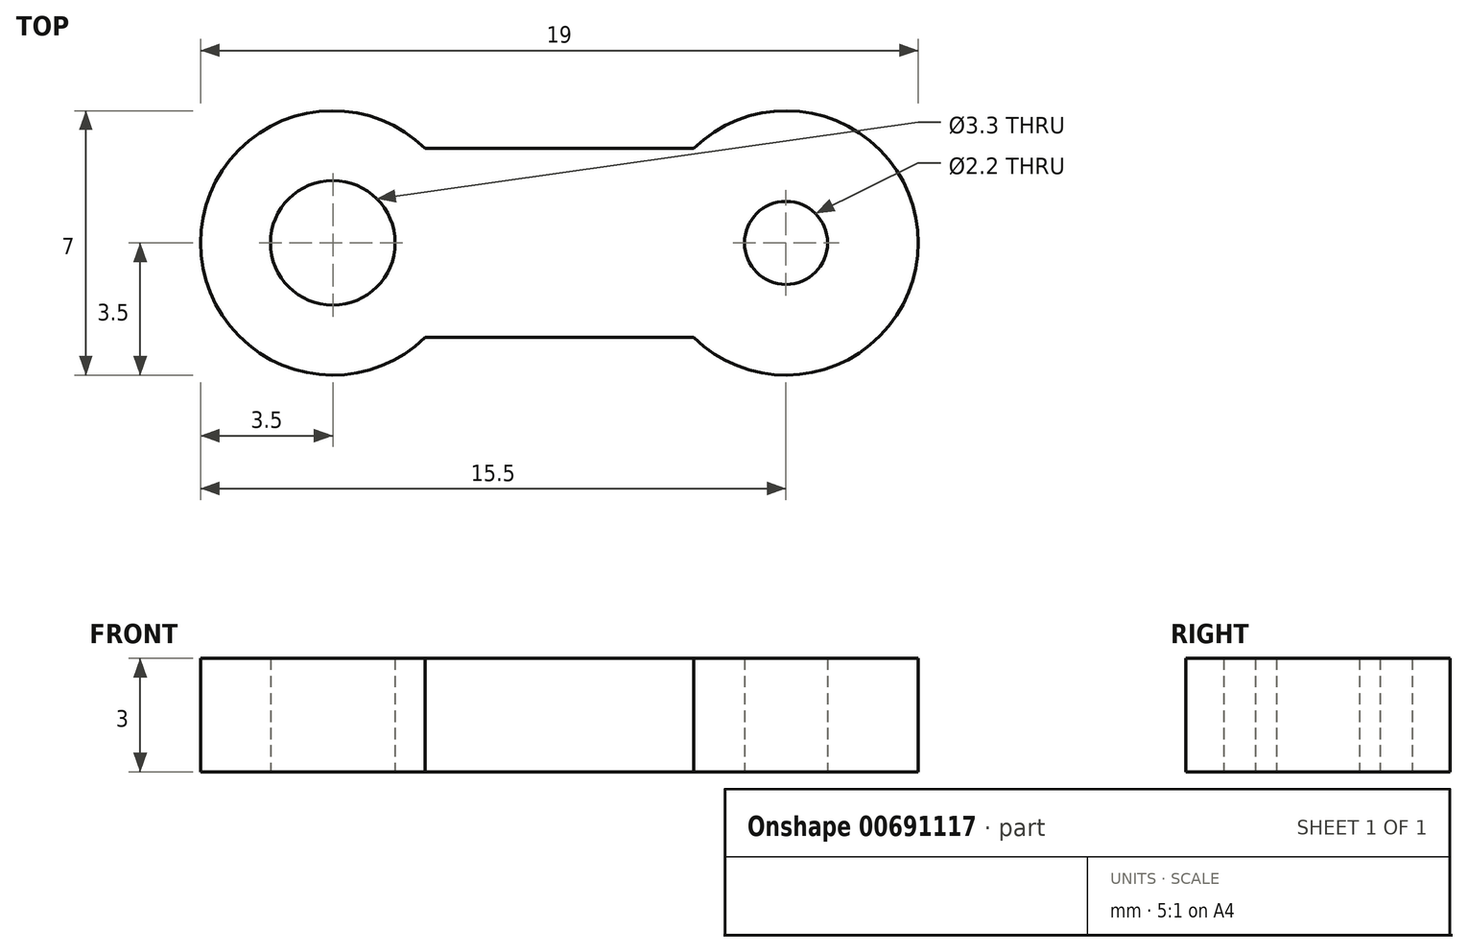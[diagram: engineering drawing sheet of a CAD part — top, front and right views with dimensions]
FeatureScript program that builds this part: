
annotation { "Feature Type Name" : "Feature", "Feature Type Description" : "" }
export const myFeature = defineFeature(function(context is Context, id is Id, definition is map)
    precondition{}
    {
        {
            var Q0;
            Q0=qCreatedBy(makeId("Top.planeOp"),FACE);
            var sketch = newSketch(context, id + "F0", { "sketchPlane" : qUnion([Q0])});
            skLineSegment(sketch, "E0", {"start": v(-6, 0) * mm, "end": v(6, 0) * mm, "construction": true});
            skArc(sketch, "E1", {"start": v(-3.55, 2.5) * mm, "mid": v(-9.5, 0) * mm, "end": v(-3.55, -2.5) * mm});
            skArc(sketch, "E2", {"start": v(3.55, -2.5) * mm, "mid": v(9.5, 0) * mm, "end": v(3.55, 2.5) * mm});
            skLineSegment(sketch, "E3", {"start": v(-3.55, 2.5) * mm, "end": v(3.55, 2.5) * mm});
            skLineSegment(sketch, "E4.MirrorCS", {"start": v(-3.55, -2.5) * mm, "end": v(3.55, -2.5) * mm});
            skCircle(sketch, "E5", {"center": v(-6, 0) * mm, "radius": 1.65 * mm});
            skCircle(sketch, "E6", {"center": v(6, 0) * mm, "radius": 1.1 * mm});
            skSolve(sketch);
        }
        {
            var Q0;
            Q0=makeQuery(id+"F0.imprint","IMPRINT",FACE,{"disambiguationData":[TD([[makeQuery(id+"F0.imprint","IMPRINT",EDGE,{"derivedFrom":sQuery(id+"F0.wireOp",EDGE,"E1")}),1.0]])]});
            extrude(context, id + "F1", {"entities" : qUnion([Q0]), "depth" : 3 * mm, "offsetDistance" : 25 * mm});
        }
    });
